# Revit family: SH -666A-12W
name_source: partatom
category: Lighting Fixtures
revit_build: Autodesk Revit 2017 (Build: 20160225_1515(x64)
units: mm (PartAtom-declared; Revit-internal decimal feet)

## family parameters
Always vertical = Yes
Cut with Voids When Loaded = No
Host = Wall
Light Source = Yes
OmniClass Number = 23.80.70.00
OmniClass Title = Lighting
Part Type = Normal
Room Calculation Point = No
Round Connector Dimension = Use Diameter
Shared = Yes

## types (1)
- SH-666A-12W-Aluminum(White color-4000K-LED)
    Body Material = Aluminum
    Body color = White
    Color Filter = 16777215
    Cost = 0 $
    Cunsumption current = 0 A
    Dimming Lamp Color Temperature Shift = <None>
    Emit Shape Visible in Rendering = No
    Emit from Rectangle Length = 60.0 cm
    Emit from Rectangle Width = 2.0 cm
    IP = IP20
    Instalation = Wall mounted
    Lamp = LED
    Manufacturer = SHOA
    Model = SH-666A-12W
    Photometric Web File = generic
    Protection Class = class I
    Tilt Angle = 60.00°
    Type medule = SMD
    URL = https://www.shoaco.com
    Voltage/Frequency = 230V/50HZ
    Website = www.shoaco.com
    color temperature = 4000K
    wattage = 12 W

## geometry (parser evidence)
native form markers: Sweep x2
no freeform markers — native parametric forms only
